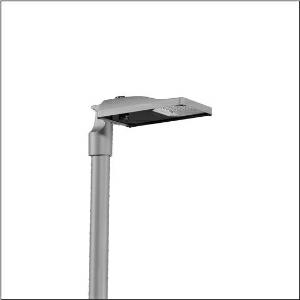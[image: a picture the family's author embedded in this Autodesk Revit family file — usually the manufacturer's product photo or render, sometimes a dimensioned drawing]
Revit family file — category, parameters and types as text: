
# Revit family: streetlight_sl_31_micro___st1_0a_5xh1d71t08da_c755
name_source: partatom
category: Lighting Fixtures
units: mm (PartAtom-declared; Revit-internal decimal feet)

## family parameters
Cut with Voids When Loaded = No
Host = Face
Light Source = No
Part Type = Normal
Room Calculation Point = No
Round Connector Dimension = Use Diameter
Shared = No

## types (1)
- --- (1 x LED, 3990 lm, 37.7 W, 2200K)
    Apparent Load = 38 VA
    CIE Flux Codes = 37 72 97 100 100
    Color Rendering = 70
    Color Temperature = 2200K
    Default Elevation = 1800 mm
    Description = Streetlight SL 31 micro D4i, Desk-Remote mast luminaire for post-top, side-entry; light control with lens of PMMA; light distribution: ST1.0a, direct asymmetric distribution, for standard-compliant lighting for roads and squares; LED: luminous flux: 3.990lm, light colour: 722, colour temperature: 2200K; luminous efficacy: 105,8lm/W; control: pre-setting: logarithmic dimming characteristic, flexible luminous flux parameterisation, time-dependent luminous flux control, constant luminous flux control, power reduction, intelligent temperature release in ECG and LED module, overheat protection; luminaire housing, of diecast aluminium, SITECO metallic grey (DB 702S), corrosivity category C5 high according to DIN EN ISO 12944; cover of toughened safety glass, transparent, mast flange of diecast aluminium, SITECO metallic grey (DB 702S), spigot size: 76/60mm, mast flange included unmounted; cable length: 6,5m, connection cable pre-assembled; mains connection: 220..240V, AC, 50/60Hz; power consumption (at start of service life): 37,7W / (at end of service life): 40,9W / (with reduced operation 50%): 16,3W; protection rating (complete): IP66; insulation class (complete): insulation class II (safety insulation); impact resistance: IK09; certification: CE, ENEC, ENEC+, VDE, UKCA, ZD4i; permissible operating ambient temperature for outdoor applications: -40..+50°C; packaging unit: 1 piece

Light Distribution: ST1.0a
    Height = 76 mm
    Lamp = 1 x LED
    Lamp Light Flux = 3990 lm
    Lamp Power = 37.7 W
    Lamp count = 1
    Length = 467 mm
    Luminous efficacy = 106 lm/W
    Manufacturer = Siteco
    ModVariant = No
    Model = 5XH1D71T08DA
    Number of Poles = 1
    OnlyDefault = Yes
    Power Factor = 1
    Product Name = Streetlight SL 31 micro | ST1.0a
    Product group = mast luminaire | pylon top
    ProductGroupID = 6100
    Protection Class = Protection class II
    Protection Degree = IP 66
    RLX_Detail_Level = 1
    RLX_Emergency_Light_Flux = 0 lm
    RLX_Emergency_Type = 0
    RLX_Emergency_Type_DB = No
    RlxData = <blob elided: 23313 chars, md5=4b0551cd>
    Socket = socket
    Standby Power = 0 W
    System Light Flux = 3990 lm
    System Power = 38 W
    Type Comments = factory setting: luminous flux: 100 % | dim-lin: 254 | 745 mA
    Type Image = l_1300315.jpg
    URL = http://relux.com
    VarID = @adj_009515
    Voltage = 0 V
    Weight = 0.00 kg
    Width = 265 mm

## geometry (parser evidence)
native form markers: Blend x4, Sweep x9
no freeform markers — native parametric forms only
